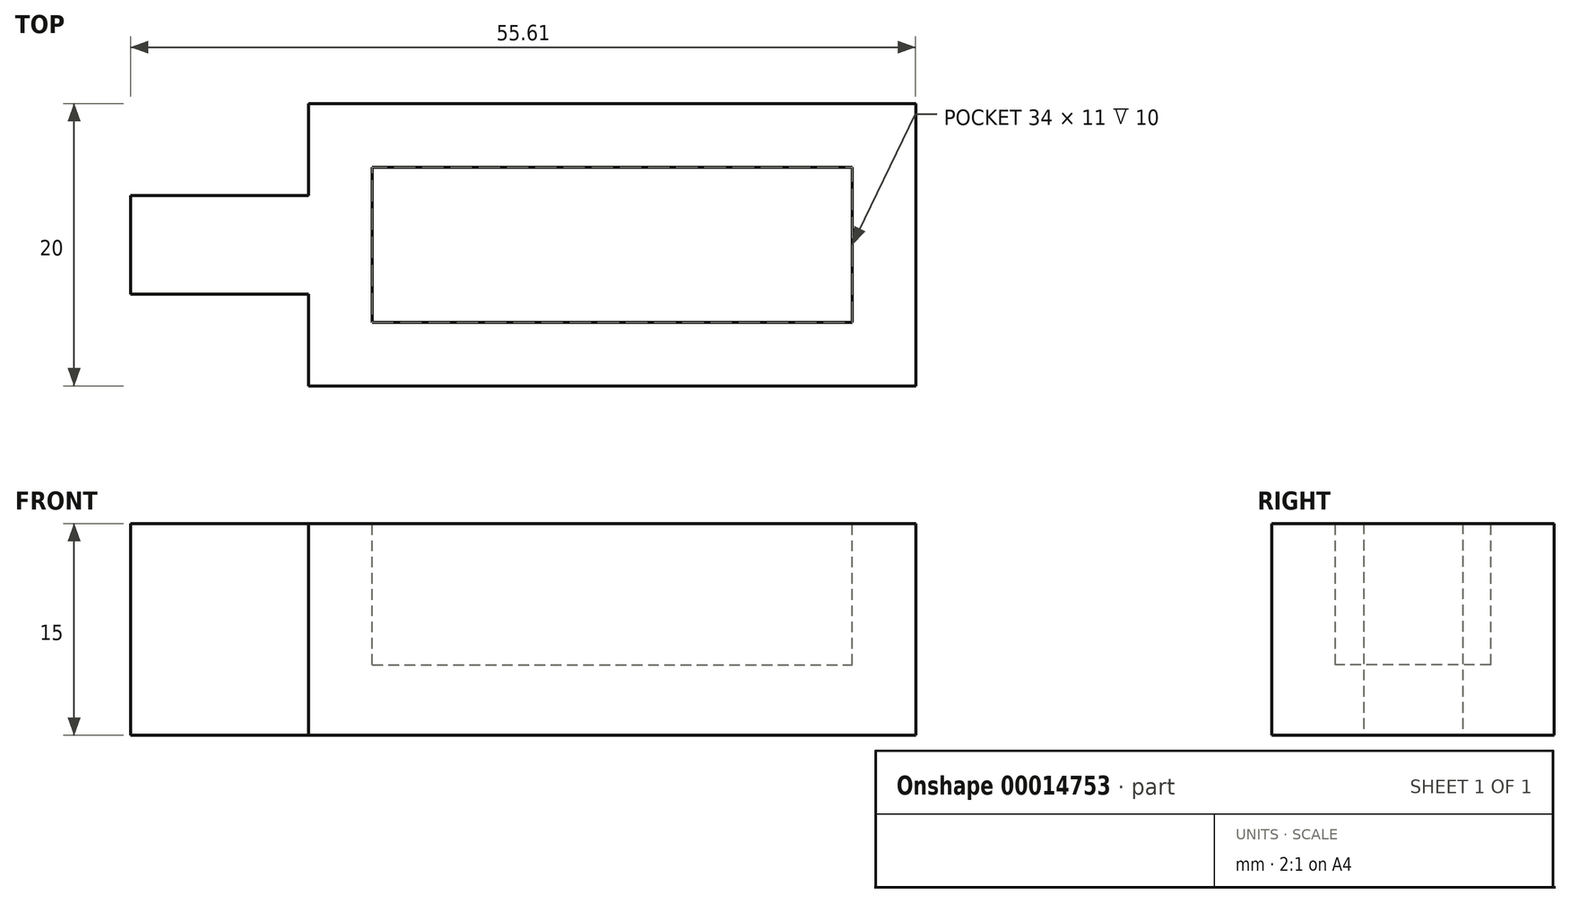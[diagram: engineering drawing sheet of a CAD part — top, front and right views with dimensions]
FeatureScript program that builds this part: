
annotation { "Feature Type Name" : "Feature", "Feature Type Description" : "" }
export const myFeature = defineFeature(function(context is Context, id is Id, definition is map)
    precondition{}
    {
        {
            var Q0;
            Q0=qCreatedBy(makeId("Top.planeOp"),FACE);
            var sketch = newSketch(context, id + "F0", { "sketchPlane" : qUnion([Q0])});
            skLineSegment(sketch, "E0", {"start": v(-25.3, 11.35) * mm, "end": v(17.7, 11.35) * mm});
            skLineSegment(sketch, "E1", {"start": v(17.7, 11.35) * mm, "end": v(17.7, -8.65) * mm});
            skLineSegment(sketch, "E2", {"start": v(17.7, -8.65) * mm, "end": v(-25.3, -8.65) * mm});
            skLineSegment(sketch, "E3", {"start": v(-25.3, -8.65) * mm, "end": v(-25.3, -2.15) * mm});
            skLineSegment(sketch, "E4", {"start": v(-25.3, -2.15) * mm, "end": v(-37.92, -2.15) * mm});
            skLineSegment(sketch, "E5", {"start": v(-37.92, -2.15) * mm, "end": v(-37.92, 4.85) * mm});
            skLineSegment(sketch, "E6", {"start": v(-37.92, 4.85) * mm, "end": v(-25.3, 4.85) * mm});
            skLineSegment(sketch, "E7", {"start": v(-25.3, 4.85) * mm, "end": v(-25.3, 11.35) * mm});
            skSolve(sketch);
        }
        {
            var Q0;
            Q0=makeQuery(id+"F0.imprint","IMPRINT",FACE,{"disambiguationData":[TD([[makeQuery(id+"F0.imprint","IMPRINT",EDGE,{"derivedFrom":sQuery(id+"F0.wireOp",EDGE,"E0")}),-1.0]])]});
            extrude(context, id + "F1", {"entities" : qUnion([Q0]), "depth" : 15 * mm});
        }
        {
            var Q0;
            Q0=makeQuery(id+"F1.opExtrude","CAP_FACE",FACE,{"disambiguationData":[OSD([sQuery(id+"F0.wireOp",EDGE,"E0"),sQuery(id+"F0.wireOp",EDGE,"E1"),sQuery(id+"F0.wireOp",EDGE,"E2"),sQuery(id+"F0.wireOp",EDGE,"E3"),sQuery(id+"F0.wireOp",EDGE,"E4"),sQuery(id+"F0.wireOp",EDGE,"E5"),sQuery(id+"F0.wireOp",EDGE,"E6"),sQuery(id+"F0.wireOp",EDGE,"E7")])],"isStart":false});
            var sketch = newSketch(context, id + "F2", { "sketchPlane" : qUnion([Q0])});
            skLineSegment(sketch, "E8.bottom", {"start": v(-20.8, 6.85) * mm, "end": v(13.2, 6.85) * mm});
            skLineSegment(sketch, "E8.top", {"start": v(-20.8, -4.15) * mm, "end": v(13.2, -4.15) * mm});
            skLineSegment(sketch, "E8.left", {"start": v(-20.8, 6.85) * mm, "end": v(-20.8, -4.15) * mm});
            skLineSegment(sketch, "E8.right", {"start": v(13.2, 6.85) * mm, "end": v(13.2, -4.15) * mm});
            skSolve(sketch);
        }
        {
            var Q0;
            Q0=makeQuery(id+"F2.imprint","IMPRINT",FACE,{"disambiguationData":[TD([[makeQuery(id+"F2.imprint","IMPRINT",EDGE,{"derivedFrom":sQuery(id+"F2.wireOp",EDGE,"E8.bottom")}),-1.0]])]});
            extrude(context, id + "F3", {"entities" : qUnion([Q0]), "operationType" : NewBodyOperationType.REMOVE, "oppositeDirection" : true, "depth" : 10 * mm});
        }
    });
